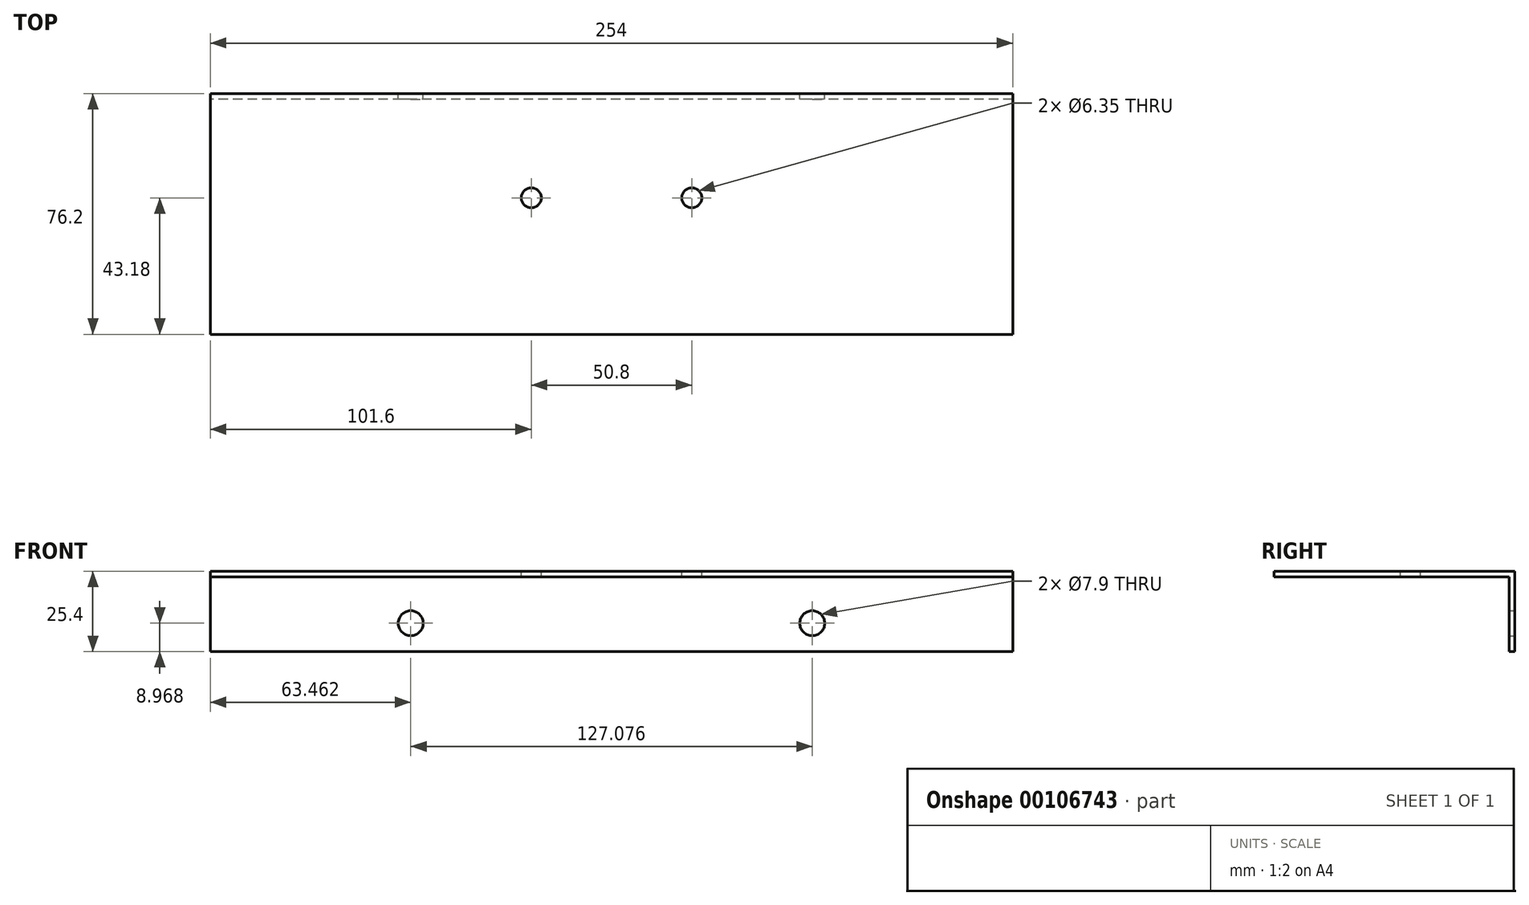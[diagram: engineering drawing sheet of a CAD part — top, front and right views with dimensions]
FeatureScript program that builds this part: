
annotation { "Feature Type Name" : "Feature", "Feature Type Description" : "" }
export const myFeature = defineFeature(function(context is Context, id is Id, definition is map)
    precondition{}
    {
        {
            var Q0;
            Q0=qCreatedBy(makeId("Right.planeOp"),FACE);
            var sketch = newSketch(context, id + "F0", { "sketchPlane" : qUnion([Q0])});
            skLineSegment(sketch, "E0.bottom", {"start": v(36.3, -0.9) * mm, "end": v(-38.1, -0.9) * mm});
            skLineSegment(sketch, "E0.top", {"start": v(38.1, 0.9) * mm, "end": v(-38.1, 0.9) * mm});
            skLineSegment(sketch, "E0.left", {"start": v(38.1, -0.9) * mm, "end": v(38.1, 0.9) * mm});
            skLineSegment(sketch, "E0.right", {"start": v(-38.1, -0.9) * mm, "end": v(-38.1, 0.9) * mm});
            skPoint(sketch, "E0.middle", {"position": v(0, 0) * mm});
            skLineSegment(sketch, "E1", {"start": v(38.1, -0.9) * mm, "end": v(38.1, -24.5) * mm});
            skLineSegment(sketch, "E2", {"start": v(38.1, -24.5) * mm, "end": v(36.3, -24.5) * mm});
            skLineSegment(sketch, "E3", {"start": v(36.3, -24.5) * mm, "end": v(36.3, -0.9) * mm});
            skSolve(sketch);
        }
        {
            var Q0;
            Q0 = qSketchRegion(id + "F0", true);
            extrude(context, id + "F1", {"entities" : qUnion([Q0]), "depth" : 127 * mm, "hasSecondDirection" : true, "secondDirectionOppositeDirection" : true, "secondDirectionDepth" : 127 * mm});
        }
        {
            var Q0;
            Q0=makeQuery(id+"F1.opExtrude","SWEPT_FACE",FACE,{"disambiguationData":[OSD([sQuery(id+"F0.wireOp",EDGE,"E0.top")])]});
            var sketch = newSketch(context, id + "F2", { "sketchPlane" : qUnion([Q0])});
            skCircle(sketch, "E4", {"center": v(-25.4, 5.08) * mm, "radius": 3.18 * mm});
            skCircle(sketch, "E5", {"center": v(25.4, 5.08) * mm, "radius": 3.18 * mm});
            skSolve(sketch);
        }
        {
            var Q0;
            Q0 = qSketchRegion(id + "F2", true);
            extrude(context, id + "F3", {"entities" : qUnion([Q0]), "operationType" : NewBodyOperationType.REMOVE, "endBound" : BoundingType.THROUGH_ALL, "oppositeDirection" : true, "depth" : 25.4 * mm});
        }
        {
            var Q0;
            Q0=makeQuery(id+"F1.opExtrude","SWEPT_FACE",FACE,{"disambiguationData":[OSD([sQuery(id+"F0.wireOp",EDGE,"E0.left"),sQuery(id+"F0.wireOp",EDGE,"E1")])]});
            var sketch = newSketch(context, id + "F4", { "sketchPlane" : qUnion([Q0])});
            skPoint(sketch, "E6", {"position": v(-63.54, -15.53) * mm});
            skPoint(sketch, "E7", {"position": v(63.54, -15.53) * mm});
            skSolve(sketch);
        }
        {
            var Q0;
            Q0=sQuery(id+"F4.wireOp",VERTEX,"E6");
            var Q1;
            Q1=sQuery(id+"F4.wireOp",VERTEX,"E7");
            var Q2;
            Q2=makeQuery(id+"F1.opExtrude","SWEPT_BODY",BODY,{"disambiguationData":[OSD([sQuery(id+"F0.wireOp",EDGE,"E0.bottom"),sQuery(id+"F0.wireOp",EDGE,"E0.top"),sQuery(id+"F0.wireOp",EDGE,"E0.left"),sQuery(id+"F0.wireOp",EDGE,"E0.right"),sQuery(id+"F0.wireOp",EDGE,"E1"),sQuery(id+"F0.wireOp",EDGE,"E2"),sQuery(id+"F0.wireOp",EDGE,"E3")])]});
            hole(context, id + "F5", {"style" : HoleStyle.SIMPLE, "endStyle" : HoleEndStyle.BLIND, "holeDiameter" : 7.9 * mm, "holeDepth" : 12.7 * mm, "startFromSketch" : true, "locations" : qUnion([Q0, Q1]), "scope" : qUnion([Q2])});
        }
    });
